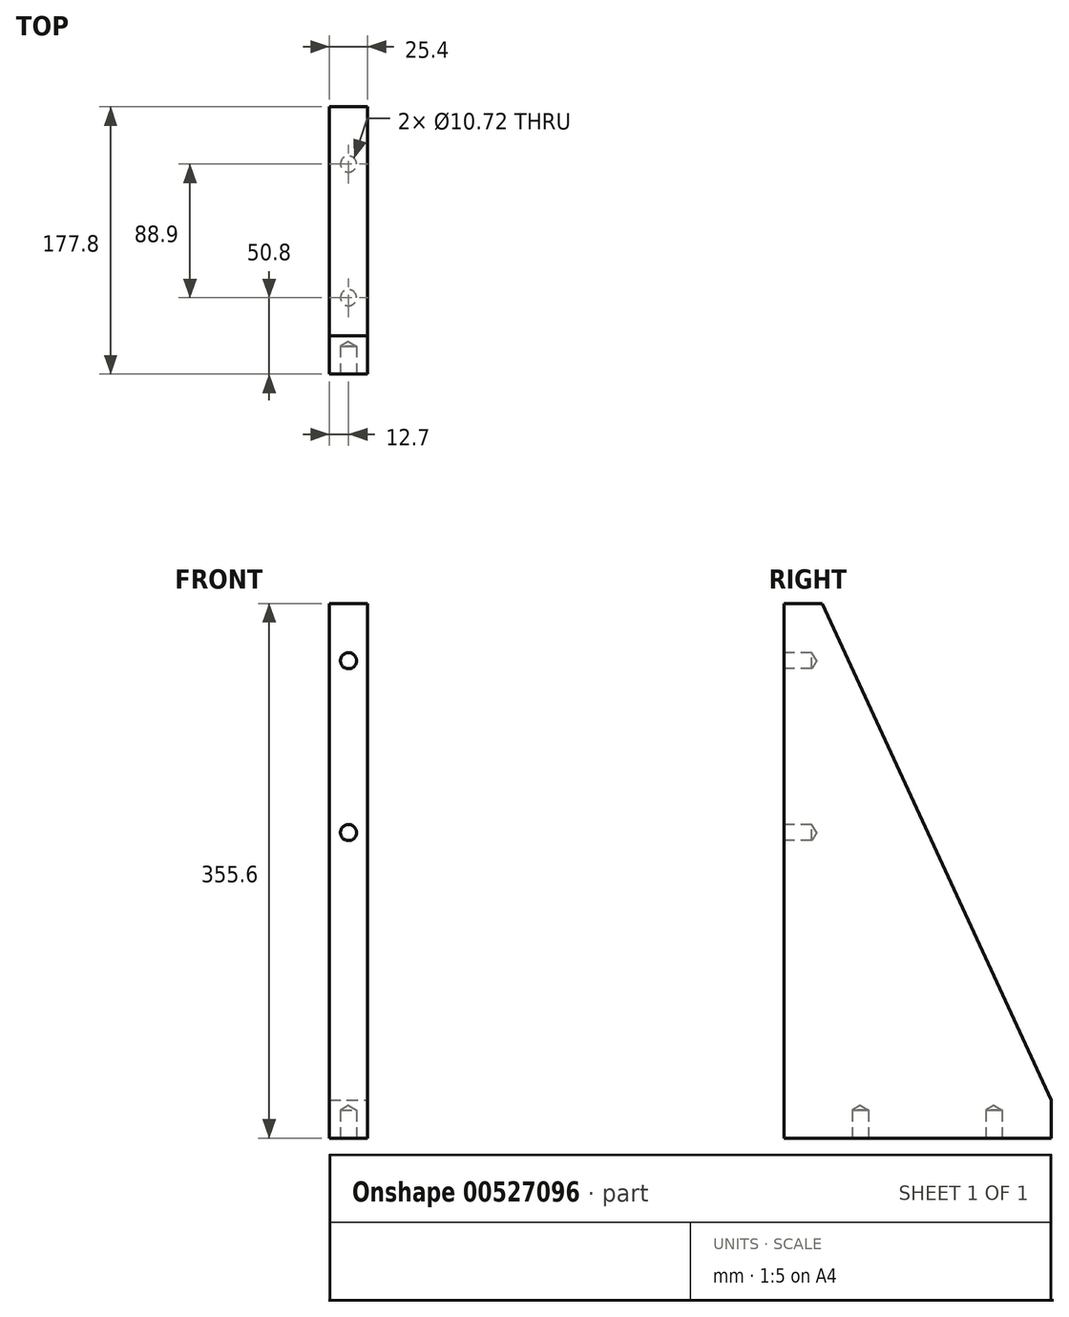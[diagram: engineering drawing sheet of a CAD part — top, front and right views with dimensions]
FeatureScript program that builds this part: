
annotation { "Feature Type Name" : "Feature", "Feature Type Description" : "" }
export const myFeature = defineFeature(function(context is Context, id is Id, definition is map)
    precondition{}
    {
        {
            var Q0;
            Q0=qCreatedBy(makeId("Right.planeOp"),FACE);
            var sketch = newSketch(context, id + "F0", { "sketchPlane" : qUnion([Q0])});
            skLineSegment(sketch, "E0", {"start": v(0, 0) * mm, "end": v(0, 355.6) * mm});
            skLineSegment(sketch, "E1", {"start": v(0, 355.6) * mm, "end": v(25.4, 355.6) * mm});
            skLineSegment(sketch, "E2", {"start": v(177.8, 0) * mm, "end": v(0, 0) * mm});
            skLineSegment(sketch, "E3", {"start": v(177.8, 0) * mm, "end": v(177.8, 25.4) * mm});
            skLineSegment(sketch, "E4", {"start": v(177.8, 25.4) * mm, "end": v(25.4, 355.6) * mm});
            skSolve(sketch);
        }
        {
            var Q0;
            Q0=makeQuery(id+"F0.imprint","IMPRINT",FACE,{"disambiguationData":[TD([[makeQuery(id+"F0.imprint","IMPRINT",EDGE,{"derivedFrom":sQuery(id+"F0.wireOp",EDGE,"E0")}),-1.0]])]});
            extrude(context, id + "F1", {"entities" : qUnion([Q0]), "oppositeDirection" : true, "depth" : 25.4 * mm, "offsetDistance" : 25.4 * mm});
        }
        {
            var Q0;
            Q0=makeQuery(id+"F1.opExtrude","SWEPT_FACE",FACE,{"disambiguationData":[OSD([sQuery(id+"F0.wireOp",EDGE,"E0")])]});
            var sketch = newSketch(context, id + "F2", { "sketchPlane" : qUnion([Q0])});
            skPoint(sketch, "E5", {"position": v(-12.7, 317.5) * mm});
            skPoint(sketch, "E6", {"position": v(-12.7, 203.2) * mm});
            skPoint(sketch, "E7", {"position": v(-12.7, 0) * mm});
            skSolve(sketch);
        }
        {
            var Q0;
            Q0=sQuery(id+"F2.wireOp",VERTEX,"E5");
            var Q1;
            Q1=sQuery(id+"F2.wireOp",VERTEX,"E6");
            var Q2;
            Q2=makeQuery(id+"F1.opExtrude","SWEPT_BODY",BODY,{"disambiguationData":[OSD([sQuery(id+"F0.wireOp",EDGE,"E0"),sQuery(id+"F0.wireOp",EDGE,"E1"),sQuery(id+"F0.wireOp",EDGE,"AOI8VjUK-K7eE-hyjh-rK6C-JEebZhXrhw5d"),sQuery(id+"F0.wireOp",EDGE,"E2")])]});
            hole(context, id + "F3", {"style" : HoleStyle.SIMPLE, "endStyle" : HoleEndStyle.BLIND, "standardTappedOrClearance" : lookupTablePath({ "standard" : "ANSI", "engagement" : "75%", "pitch" : "13 tpi", "size" : "1/2", "type" : "Tapped" }), "standardBlindInLast" : lookupTablePath({ "standard" : "ANSI", "engagement" : "75%", "pitch" : "13 tpi", "size" : "1/2", "type" : "Tapped" }), "holeDiameter" : 10.72 * mm, "showTappedDepth" : true, "holeDepth" : 18.56 * mm, "isTappedThrough" : true, "tappedDepth" : 12.7 * mm, "tapClearance" : 3, "startFromSketch" : true, "locations" : qUnion([Q0, Q1]), "scope" : qUnion([Q2]), "majorDiameter" : 12.7 * mm});
        }
        {
            var Q0;
            Q0=makeQuery(id+"F1.opExtrude","SWEPT_FACE",FACE,{"disambiguationData":[OSD([sQuery(id+"F0.wireOp",EDGE,"E2")])]});
            var sketch = newSketch(context, id + "F4", { "sketchPlane" : qUnion([Q0])});
            skPoint(sketch, "E8", {"position": v(-12.7, -50.8) * mm});
            skPoint(sketch, "E9", {"position": v(-12.7, -139.7) * mm});
            skPoint(sketch, "E10", {"position": v(-12.7, 0) * mm});
            skSolve(sketch);
        }
        {
            var Q0;
            Q0=sQuery(id+"F4.wireOp",VERTEX,"E8");
            var Q1;
            Q1=sQuery(id+"F4.wireOp",VERTEX,"E9");
            var Q2;
            Q2=makeQuery(id+"F1.opExtrude","SWEPT_BODY",BODY,{"disambiguationData":[OSD([sQuery(id+"F0.wireOp",EDGE,"E0"),sQuery(id+"F0.wireOp",EDGE,"E1"),sQuery(id+"F0.wireOp",EDGE,"AOI8VjUK-K7eE-hyjh-rK6C-JEebZhXrhw5d"),sQuery(id+"F0.wireOp",EDGE,"E2")])]});
            hole(context, id + "F5", {"style" : HoleStyle.SIMPLE, "endStyle" : HoleEndStyle.BLIND, "standardTappedOrClearance" : lookupTablePath({ "standard" : "ANSI", "engagement" : "75%", "pitch" : "13 tpi", "size" : "1/2", "type" : "Tapped" }), "standardBlindInLast" : lookupTablePath({ "standard" : "ANSI", "engagement" : "75%", "pitch" : "13 tpi", "size" : "1/2", "type" : "Tapped" }), "holeDiameter" : 10.72 * mm, "showTappedDepth" : true, "holeDepth" : 18.56 * mm, "isTappedThrough" : true, "tappedDepth" : 12.7 * mm, "tapClearance" : 3, "startFromSketch" : true, "locations" : qUnion([Q0, Q1]), "scope" : qUnion([Q2]), "majorDiameter" : 12.7 * mm});
        }
    });
